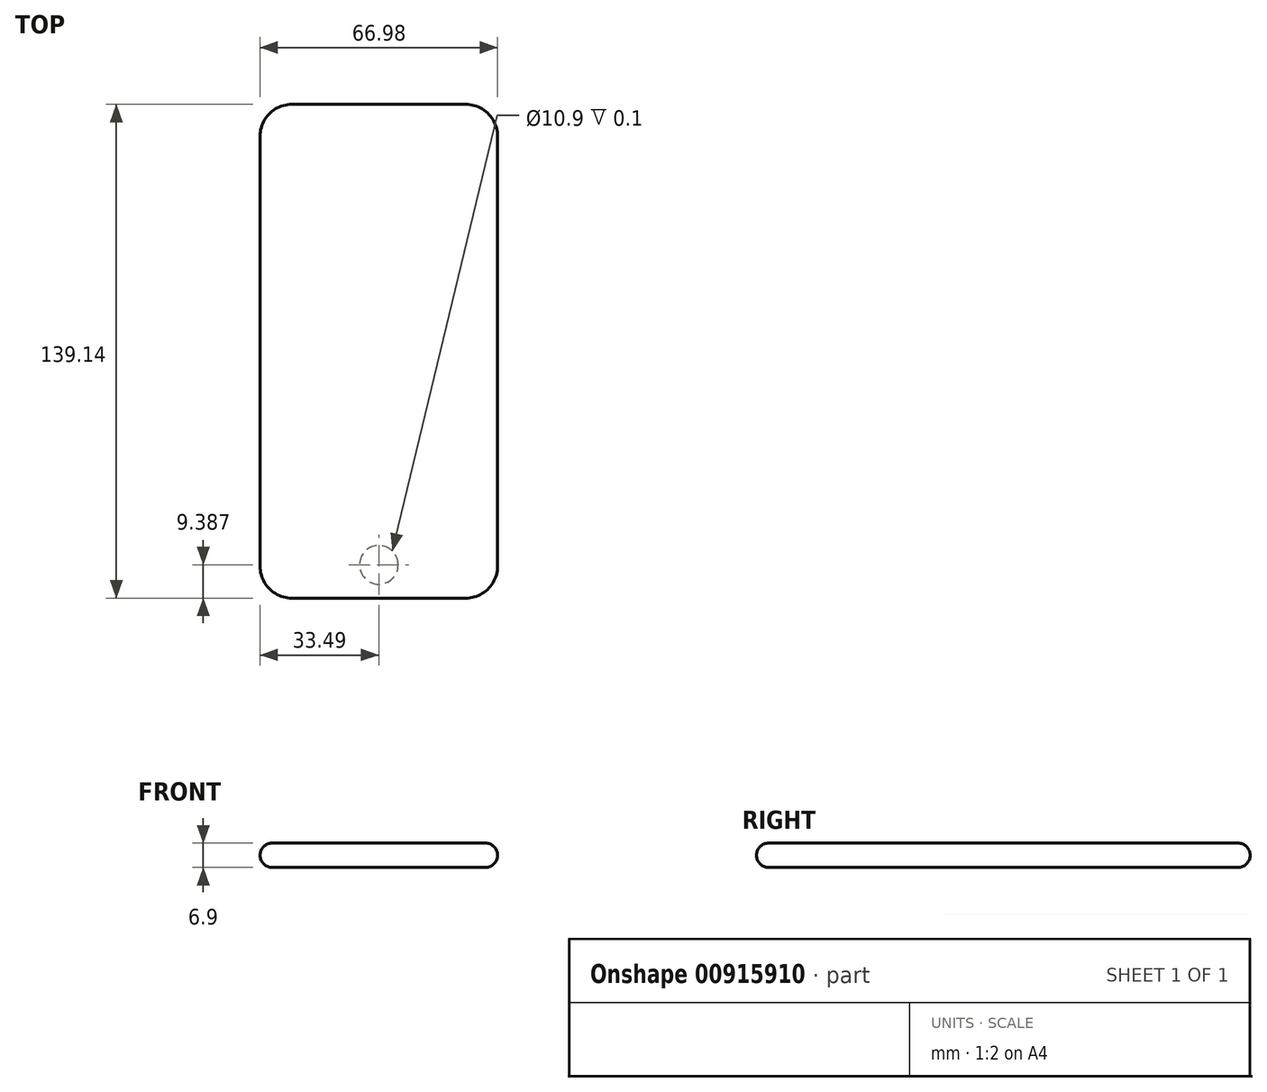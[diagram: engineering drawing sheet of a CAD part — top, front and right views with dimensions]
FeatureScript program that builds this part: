
annotation { "Feature Type Name" : "Feature", "Feature Type Description" : "" }
export const myFeature = defineFeature(function(context is Context, id is Id, definition is map)
    precondition{}
    {
        {
            var Q0;
            Q0=qCreatedBy(makeId("Top.planeOp"),FACE);
            var sketch = newSketch(context, id + "F0", { "sketchPlane" : qUnion([Q0])});
            skLineSegment(sketch, "E0.bottom", {"start": v(33.48, 69.57) * mm, "end": v(-33.48, 69.57) * mm});
            skLineSegment(sketch, "E0.top", {"start": v(33.48, -69.57) * mm, "end": v(-33.48, -69.57) * mm});
            skLineSegment(sketch, "E0.left", {"start": v(33.49, 69.57) * mm, "end": v(33.48, -69.57) * mm});
            skLineSegment(sketch, "E0.right", {"start": v(-33.48, 69.57) * mm, "end": v(-33.48, -69.57) * mm});
            skPoint(sketch, "E0.middle", {"position": v(0, 0) * mm});
            skSolve(sketch);
        }
        {
            var Q0;
            Q0 = qSketchRegion(id + "F0", true);
            extrude(context, id + "F1", {"entities" : qUnion([Q0]), "depth" : 6.9 * mm, "offsetDistance" : 25 * mm});
        }
        {
            var Q0;
            Q0=makeQuery(id+"F1.opExtrude","SWEPT_EDGE",EDGE,{"disambiguationData":[OSD([sQuery(id+"F0.wireOp",EDGE,"E0.bottom"),sQuery(id+"F0.wireOp",EDGE,"E0.right")])]});
            var Q1;
            Q1=makeQuery(id+"F1.opExtrude","SWEPT_EDGE",EDGE,{"disambiguationData":[OSD([sQuery(id+"F0.wireOp",EDGE,"E0.bottom"),sQuery(id+"F0.wireOp",EDGE,"E0.left")])]});
            var Q2;
            Q2=makeQuery(id+"F1.opExtrude","SWEPT_EDGE",EDGE,{"disambiguationData":[OSD([sQuery(id+"F0.wireOp",EDGE,"E0.top"),sQuery(id+"F0.wireOp",EDGE,"E0.left")])]});
            var Q3;
            Q3=makeQuery(id+"F1.opExtrude","SWEPT_EDGE",EDGE,{"disambiguationData":[OSD([sQuery(id+"F0.wireOp",EDGE,"E0.top"),sQuery(id+"F0.wireOp",EDGE,"E0.right")])]});
            fillet(context, id + "F2", {"entities" : qUnion([Q0, Q1, Q2, Q3]), "radius" : 9 * mm, "tangentPropagation" : true, "allowEdgeOverflow" : false});
        }
        {
            var Q0;
            Q0=makeQuery(id+"F1.opExtrude","CAP_FACE",FACE,{"disambiguationData":[OSD([sQuery(id+"F0.wireOp",EDGE,"E0.bottom"),sQuery(id+"F0.wireOp",EDGE,"E0.top"),sQuery(id+"F0.wireOp",EDGE,"E0.left"),sQuery(id+"F0.wireOp",EDGE,"E0.right")])],"isStart":false});
            var Q1;
            Q1=makeQuery(id+"F1.opExtrude","CAP_FACE",FACE,{"disambiguationData":[OSD([sQuery(id+"F0.wireOp",EDGE,"E0.bottom"),sQuery(id+"F0.wireOp",EDGE,"E0.top"),sQuery(id+"F0.wireOp",EDGE,"E0.left"),sQuery(id+"F0.wireOp",EDGE,"E0.right")])],"isStart":true});
            fillet(context, id + "F3", {"entities" : qUnion([Q0, Q1]), "radius" : 3.45 * mm, "tangentPropagation" : true, "allowEdgeOverflow" : false});
        }
        {
            var Q0;
            Q0=makeQuery(id+"F1.opExtrude","CAP_FACE",FACE,{"disambiguationData":[OSD([sQuery(id+"F0.wireOp",EDGE,"E0.bottom"),sQuery(id+"F0.wireOp",EDGE,"E0.top"),sQuery(id+"F0.wireOp",EDGE,"E0.left"),sQuery(id+"F0.wireOp",EDGE,"E0.right")])],"isStart":true});
            var sketch = newSketch(context, id + "F4", { "sketchPlane" : qUnion([Q0])});
            skCircle(sketch, "E1", {"center": v(0, 60.18) * mm, "radius": 5.45 * mm});
            skSolve(sketch);
        }
        {
            var Q0;
            Q0 = qSketchRegion(id + "F4", true);
            extrude(context, id + "F5", {"entities" : qUnion([Q0]), "operationType" : NewBodyOperationType.REMOVE, "oppositeDirection" : true, "depth" : .1 * mm, "offsetDistance" : 25 * mm});
        }
    });
